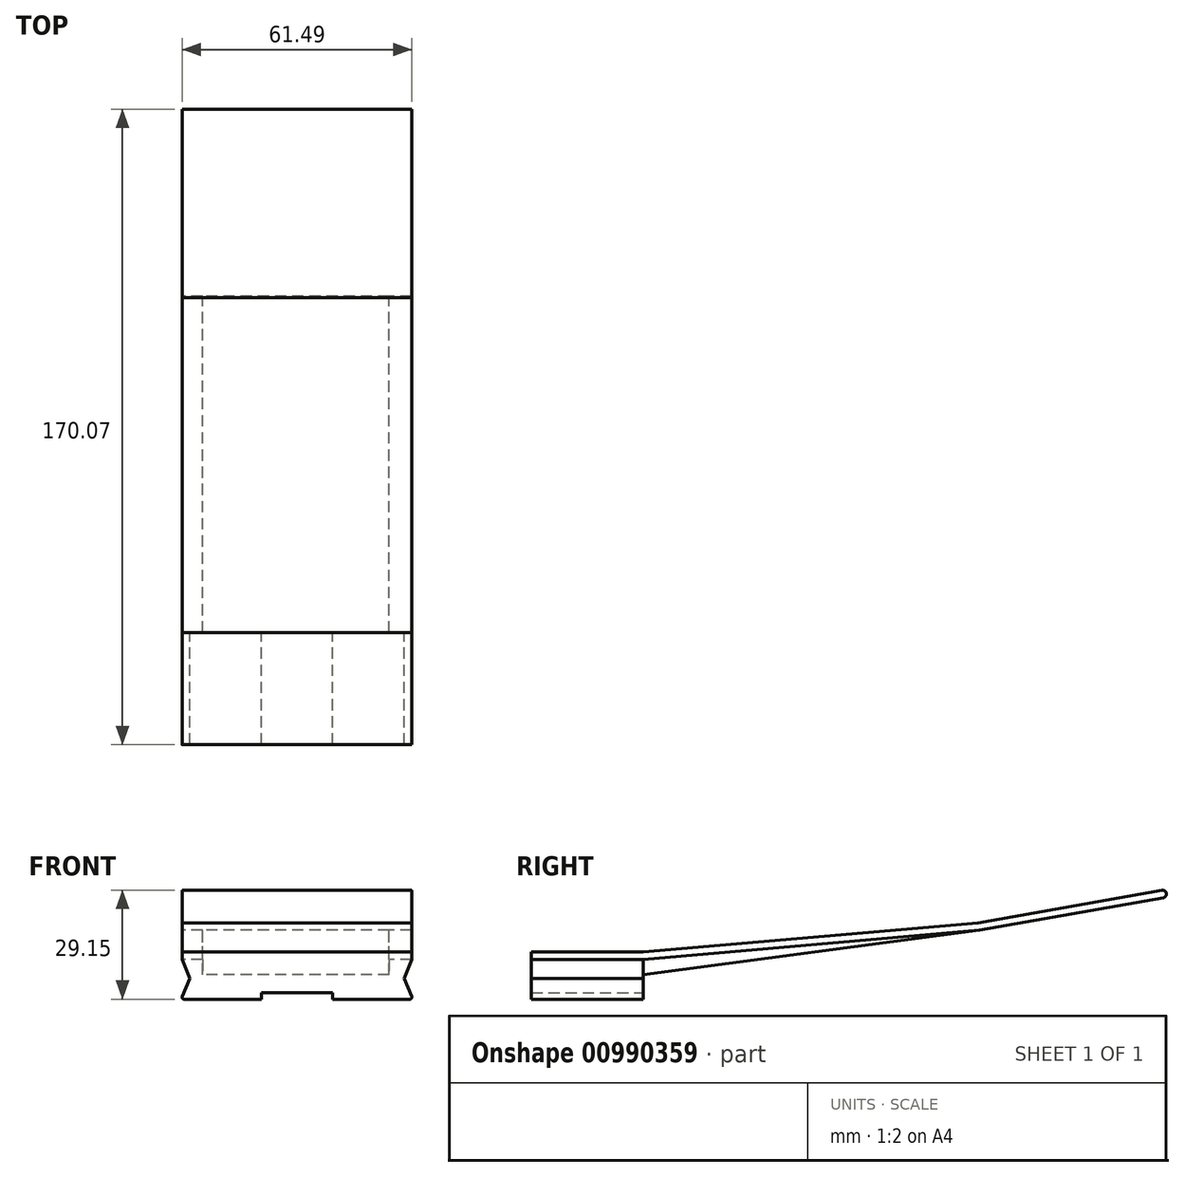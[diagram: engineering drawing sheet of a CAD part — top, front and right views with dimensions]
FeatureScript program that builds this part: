
annotation { "Feature Type Name" : "Feature", "Feature Type Description" : "" }
export const myFeature = defineFeature(function(context is Context, id is Id, definition is map)
    precondition{}
    {
        {
            var Q0;
            Q0=qCreatedBy(makeId("Front.planeOp"),FACE);
            var sketch = newSketch(context, id + "F0", { "sketchPlane" : qUnion([Q0])});
            skLineSegment(sketch, "E0", {"start": v(-39.13, 9.76) * mm, "end": v(-37.07, 14.57) * mm});
            skLineSegment(sketch, "E1", {"start": v(20.23, 14.57) * mm, "end": v(22.28, 9.76) * mm});
            skPoint(sketch, "E2.visualSharp", {"position": v(22.58, 9.07) * mm});
            skArc(sketch, "E2.filletArc", {"start": v(21.82, 9.07) * mm, "mid": v(22.24, 9.29) * mm, "end": v(22.28, 9.76) * mm});
            skPoint(sketch, "E3.visualSharp", {"position": v(-39.42, 9.07) * mm});
            skArc(sketch, "E3.filletArc", {"start": v(-39.13, 9.76) * mm, "mid": v(-39.08, 9.29) * mm, "end": v(-38.67, 9.07) * mm});
            skLineSegment(sketch, "E4", {"start": v(-38.67, 9.07) * mm, "end": v(-17.97, 9.07) * mm});
            skLineSegment(sketch, "E5", {"start": v(-17.97, 9.07) * mm, "end": v(-17.97, 10.77) * mm});
            skLineSegment(sketch, "E6", {"start": v(1.12, 10.77) * mm, "end": v(1.12, 9.07) * mm});
            skLineSegment(sketch, "E7", {"start": v(1.12, 9.07) * mm, "end": v(21.82, 9.07) * mm});
            skLineSegment(sketch, "E8", {"start": v(-17.97, 10.77) * mm, "end": v(1.12, 10.77) * mm});
            skLineSegment(sketch, "E9", {"start": v(-39.13, 21.68) * mm, "end": v(22.28, 21.68) * mm});
            skLineSegment(sketch, "E10", {"start": v(22.28, 21.68) * mm, "end": v(22.28, 19.68) * mm});
            skLineSegment(sketch, "E11", {"start": v(20.23, 14.57) * mm, "end": v(22.28, 19.68) * mm});
            skLineSegment(sketch, "E12", {"start": v(-39.13, 21.68) * mm, "end": v(-39.13, 19.68) * mm});
            skLineSegment(sketch, "E13", {"start": v(-39.13, 19.68) * mm, "end": v(-37.07, 14.57) * mm});
            skLineSegment(sketch, "E14", {"start": v(-39.13, 19.68) * mm, "end": v(22.28, 19.68) * mm});
            skSolve(sketch);
        }
        {
            var Q0;
            Q0=makeQuery(id+"F0.imprint","IMPRINT",FACE,{"disambiguationData":[TD([[makeQuery(id+"F0.imprint","IMPRINT",EDGE,{"derivedFrom":sQuery(id+"F0.wireOp",EDGE,"E0")}),-1.0]])]});
            var Q1;
            Q1=makeQuery(id+"F0.imprint","IMPRINT",FACE,{"disambiguationData":[TD([[makeQuery(id+"F0.imprint","IMPRINT",EDGE,{"derivedFrom":sQuery(id+"F0.wireOp",EDGE,"E9")}),-1.0]])]});
            extrude(context, id + "F1", {"entities" : qUnion([Q0, Q1]), "depth" : 30 * mm, "offsetDistance" : 25 * mm});
        }
        {
            var Q0;
            Q0=makeQuery(id+"F1.opExtrude","SWEPT_FACE",FACE,{"disambiguationData":[OSD([sQuery(id+"F0.wireOp",EDGE,"E10")])]});
            cPlane(context, id + "F2", {"entities" : qUnion([Q0]), "cplaneType" : CPlaneType.OFFSET, "offset" : 31 * mm, "oppositeDirection" : true, "width" : 150 * mm, "height" : 150 * mm});
        }
        {
            var Q0;
            Q0=qCreatedBy(id+"F2.planeOp",FACE);
            var sketch = newSketch(context, id + "F3", { "sketchPlane" : qUnion([Q0])});
            skLineSegment(sketch, "E15", {"start": v(89.66, 29.52) * mm, "end": v(0, 21.68) * mm});
            skLineSegment(sketch, "E16", {"start": v(0, 21.68) * mm, "end": v(0, 19.68) * mm});
            skLineSegment(sketch, "E17", {"start": v(0, 19.68) * mm, "end": v(90, 27.55) * mm});
            skLineSegment(sketch, "E18", {"start": v(89.66, 29.52) * mm, "end": v(138.9, 38.2) * mm});
            skLineSegment(sketch, "E19", {"start": v(90, 27.55) * mm, "end": v(139.25, 36.23) * mm});
            skArc(sketch, "E20", {"start": v(139.25, 36.23) * mm, "mid": v(140.06, 37.4) * mm, "end": v(138.9, 38.2) * mm});
            skLineSegment(sketch, "E21", {"start": v(0, 19.68) * mm, "end": v(0, 15.68) * mm});
            skLineSegment(sketch, "E22", {"start": v(0, 15.68) * mm, "end": v(90, 27.55) * mm});
            skSolve(sketch);
        }
        {
            var Q0;
            Q0=makeQuery(id+"F3.imprint","IMPRINT",FACE,{"disambiguationData":[TD([[makeQuery(id+"F3.imprint","IMPRINT",EDGE,{"derivedFrom":sQuery(id+"F3.wireOp",EDGE,"E15")}),1.0]])]});
            var Q1;
            Q1=sQuery(id+"F0.wireOp",VERTEX,"E9.end");
            var Q2;
            Q2=sQuery(id+"F0.wireOp",VERTEX,"E9.start");
            extrude(context, id + "F4", {"entities" : qUnion([Q0]), "operationType" : NewBodyOperationType.ADD, "endBound" : BoundingType.UP_TO_VERTEX, "depth" : 25 * mm, "endBoundEntityVertex" : qUnion([Q1]), "offsetDistance" : 25 * mm, "hasSecondDirection" : true, "secondDirectionBound" : SecondDirectionBoundingType.UP_TO_VERTEX, "secondDirectionOppositeDirection" : true, "secondDirectionDepth" : 25 * mm, "secondDirectionBoundEntityVertex" : qUnion([Q2])});
        }
        {
            var Q0;
            Q0=qSketchRegion(id+"F3",true);
            extrude(context, id + "F5", {"entities" : qUnion([Q0]), "operationType" : NewBodyOperationType.ADD, "endBound" : BoundingType.SYMMETRIC, "depth" : 50 * mm, "offsetDistance" : 25 * mm});
        }
    });
